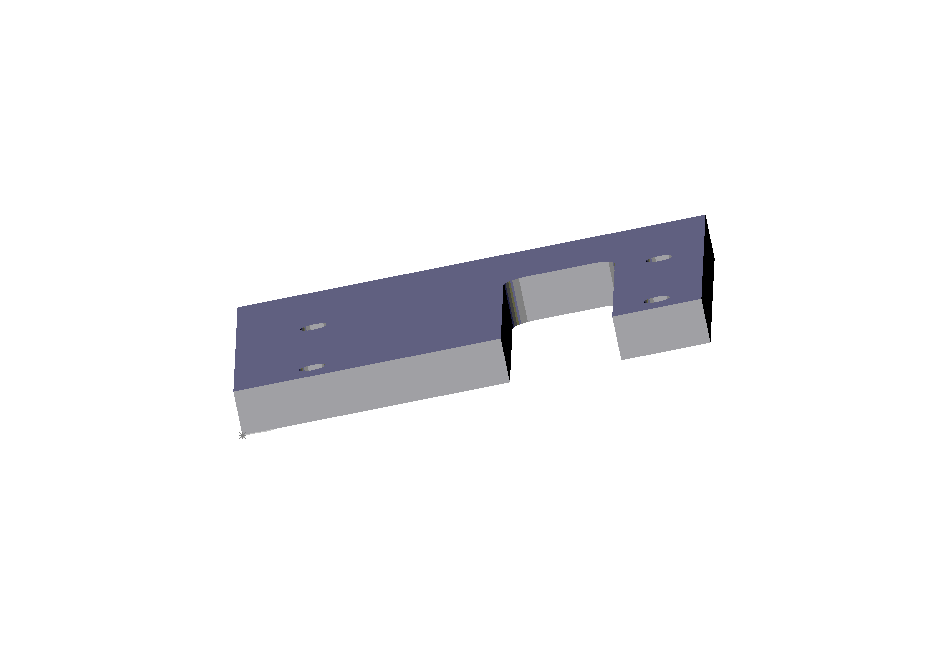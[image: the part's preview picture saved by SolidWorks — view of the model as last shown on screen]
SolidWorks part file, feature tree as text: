
SOLIDWORKS PART (.sldprt)
format: sldprt  version: not decoded by parser v0  size: 159,744 bytes
history: native  units: mm
features: sketch x173, plane x3, extrude x1 + 2 further entries (+5 scaffold rows collapsed; 18 parser-record rows omitted)
feature tree (202):
  scaffold x5  (default folders/planes/origin — collapsed)
  plane  "Plane1"
  plane  "Plane2"
  plane  "Plane3"
  sketch  "Sketch1"  dims[c1.D6=10.0mm c2.D6=10.0mm c2.D7=6.0mm c2.D10=5.0mm c2.D1=20.0mm c2.D2=60.0mm c2.D3=25.0mm c2.D4=95.0mm c2.D5=65.0mm c3.D6=17.5mm c3.D7=23.0mm c3.D8=10.0mm c3.D9=23.0mm]
  extrude  "Base-Extrude"  Depth=10mm cosMaterialEX=8300000000.0
  sketch  "cosMaterialNUXY"
  sketch  "cosMaterialGXY"
  sketch  "cosMaterialALPX"
  sketch  "cosMaterialDENS"
  sketch  "cosMaterialKX"
  sketch  "cosMaterialC"
  sketch  "Units"
  sketch  "AnalysisType"
  sketch  "MeshType"
  sketch  "cosMaterialSIGYLD"
  sketch  "cosMaterialSIGXT"
  sketch  "cosMaterialSIGXC"  dims[sMaterialName=0.0mm cosFMVItemName=0.0mm cosMaterialName=0.0mm cosComponentName=0.0mm]
  sketch  "cosMaterialEX"
  sketch  "cosMaterialNUXY"
  sketch  "cosMaterialGXY"
  sketch  "cosMaterialALPX"
  sketch  "cosMaterialDENS"
  sketch  "cosMaterialKX"
  sketch  "cosMaterialC"
  sketch  "Units"
  sketch  "AnalysisType"
  sketch  "MeshType"
  sketch  "cosMaterialSIGYLD"
  sketch  "cosMaterialSIGXT"
  sketch  "cosMaterialSIGXC"  dims[sMaterialSourceName=0.0mm sMaterialName=0.0mm cosFMVItemName=0.0mm cosMaterialName=0.0mm cosComponentName=0.0mm]
  "base:Restraint-1"
  sketch  "RestraintType"
  sketch  "Value"
  sketch  "cosRestraintComp:1"
  sketch  "cosRestraintComp:2"
  sketch  "cosRestraintComp:3"
  sketch  "cosRestraintComp:4"
  sketch  "cosRestraintComp:5"
  sketch  "cosRestraintComp:6"
  sketch  "Unit"
  sketch  "AnalysisType"
  sketch  "MeshType"
  sketch  "cosRestraintCompCheck1"
  sketch  "cosRestraintCompCheck2"
  sketch  "cosRestraintCompCheck3"
  sketch  "cosRestraintCompCheck4"
  sketch  "cosRestraintCompCheck5"
  sketch  "cosRestraintCompCheck6"
  sketch  "cosRestraintRefPlaneSet"
  sketch  "cosRestraintRefPlaneOrigin1"
  sketch  "cosRestraintRefPlaneOrigin2"
  sketch  "cosRestraintRefPlaneOrigin3"
  sketch  "cosRestraintRefPlaneXDir1"
  sketch  "cosRestraintRefPlaneXDir2"
  sketch  "cosRestraintRefPlaneXDir3"
  sketch  "cosRestraintRefPlaneNormal1"
  sketch  "cosRestraintRefPlaneNormal2"
  sketch  "cosRestraintRefPlaneNormal3"  dims[cosRestraintRefPlaneName=0.0mm]
  sketch  "cosRestraintCoordSystemType"
  sketch  "cosRestraintFaceTypeMask"  dims[cosFMVItemName=0.0mm cosRestraint4=0.0]
  sketch  "RestraintType"
  sketch  "Value"
  sketch  "cosRestraintComp:1"
  sketch  "cosRestraintComp:2"
  sketch  "cosRestraintComp:3"
  sketch  "cosRestraintComp:4"
  sketch  "cosRestraintComp:5"
  sketch  "cosRestraintComp:6"
  sketch  "Unit"
  sketch  "AnalysisType"
  sketch  "MeshType"
  sketch  "cosRestraintCompCheck1"
  sketch  "cosRestraintCompCheck2"
  sketch  "cosRestraintCompCheck3"
  sketch  "cosRestraintCompCheck4"
  sketch  "cosRestraintCompCheck5"
  sketch  "cosRestraintCompCheck6"
  sketch  "cosRestraintRefPlaneSet"
  sketch  "cosRestraintRefPlaneOrigin1"
  sketch  "cosRestraintRefPlaneOrigin2"
  sketch  "cosRestraintRefPlaneOrigin3"
  sketch  "cosRestraintRefPlaneXDir1"
  sketch  "cosRestraintRefPlaneXDir2"
  sketch  "cosRestraintRefPlaneXDir3"
  sketch  "cosRestraintRefPlaneNormal1"
  sketch  "cosRestraintRefPlaneNormal2"
  sketch  "cosRestraintRefPlaneNormal3"  dims[cosRestraintRefPlaneName=0.0mm]
  sketch  "cosRestraintCoordSystemType"
  sketch  "cosRestraintFaceTypeMask"  dims[cosFMVItemName=0.0mm]
  "base:Force-1"
  sketch  "cosForceComp:1"
  sketch  "cosForceComp:2"
  sketch  "cosForceComp:3"
  sketch  "cosForceComp:4"
  sketch  "cosForceComp:5"
  sketch  "cosForceComp:6"
  sketch  "cosForceTorqueNF"
  sketch  "cosForceCompCheck1"
  sketch  "cosForceCompCheck2"
  sketch  "cosForceCompCheck3"
  sketch  "cosForceCompCheck4"
  sketch  "cosForceCompCheck5"
  sketch  "cosForceCompCheck6"
  sketch  "Unit"
  sketch  "AnalysisType"
  sketch  "MeshType"
  sketch  "cosForceRefPlaneSet"
  sketch  "cosForceRefPlaneOrigin1"
  sketch  "cosForceRefPlaneOrigin2"
  sketch  "cosForceRefPlaneOrigin3"
  sketch  "cosForceRefPlaneXDir1"
  sketch  "cosForceRefPlaneXDir2"
  sketch  "cosForceRefPlaneXDir3"
  sketch  "cosForceRefPlaneNormal1"
  sketch  "cosForceRefPlaneNormal2"
  sketch  "cosForceRefPlaneNormal3"  dims[cosForceRefPlaneName=0.0mm]
  sketch  "cosForceCoordSystemType"
  sketch  "cosForceType"  dims[cosFMVItemName=0.0mm]
  sketch  "cosDistributionType"  dims[cosDistributionCoordSysName=0.0mm]
  sketch  "cosDistributionCoef1"
  sketch  "cosDistributionCoef2"
  sketch  "cosDistributionCoef3"
  sketch  "cosDistributionCoef4"
  sketch  "cosDistributionCoef5"
  sketch  "cosDistributionCoef6"  dims[cosForce5=0.0]
  sketch  "cosForceComp:1"
  sketch  "cosForceComp:2"
  sketch  "cosForceComp:3"
  sketch  "cosForceComp:4"
  sketch  "cosForceComp:5"
  sketch  "cosForceComp:6"
  sketch  "cosForceTorqueNF"
  sketch  "cosForceCompCheck1"
  sketch  "cosForceCompCheck2"
  sketch  "cosForceCompCheck3"
  sketch  "cosForceCompCheck4"
  sketch  "cosForceCompCheck5"
  sketch  "cosForceCompCheck6"
  sketch  "Unit"
  sketch  "AnalysisType"
  sketch  "MeshType"
  sketch  "cosForceRefPlaneSet"
  sketch  "cosForceRefPlaneOrigin1"
  sketch  "cosForceRefPlaneOrigin2"
  sketch  "cosForceRefPlaneOrigin3"
  sketch  "cosForceRefPlaneXDir1"
  sketch  "cosForceRefPlaneXDir2"
  sketch  "cosForceRefPlaneXDir3"
  sketch  "cosForceRefPlaneNormal1"
  sketch  "cosForceRefPlaneNormal2"
  sketch  "cosForceRefPlaneNormal3"  dims[cosForceRefPlaneName=0.0mm]
  sketch  "cosForceCoordSystemType"
  sketch  "cosForceType"  dims[cosFMVItemName=0.0mm]
  sketch  "cosDistributionType"  dims[cosDistributionCoordSysName=0.0mm]
  sketch  "cosDistributionCoef1"
  sketch  "cosDistributionCoef2"
  sketch  "cosDistributionCoef3"
  sketch  "cosDistributionCoef4"
  sketch  "cosDistributionCoef5"
  sketch  "cosDistributionCoef6"
  parser-record x18  (decoder bookkeeping rows leaked as tree rows — omitted from the tree; the rows remain in map.json)
  sketch  "faceID"  dims[cosFaceID=0.0]
  sketch  "faceID"
  sketch  "faceID"
  sketch  "faceID"
  sketch  "faceID"
  sketch  "faceID"
  sketch  "faceID"
  sketch  "faceID"
  sketch  "faceID"
  sketch  "faceID"
  sketch  "faceID"
  sketch  "faceID"
  sketch  "faceID"
  sketch  "faceID"
  sketch  "faceID"
  sketch  "faceID"
  sketch  "faceID"
  sketch  "faceID"
  sketch  "faceID"
decode coverage: 16 of 174 modeling features carry decoded parameters; 2 rows unclassified (native names shown)
note: suppression state not decoded; provenance and decode notes live in map.json
